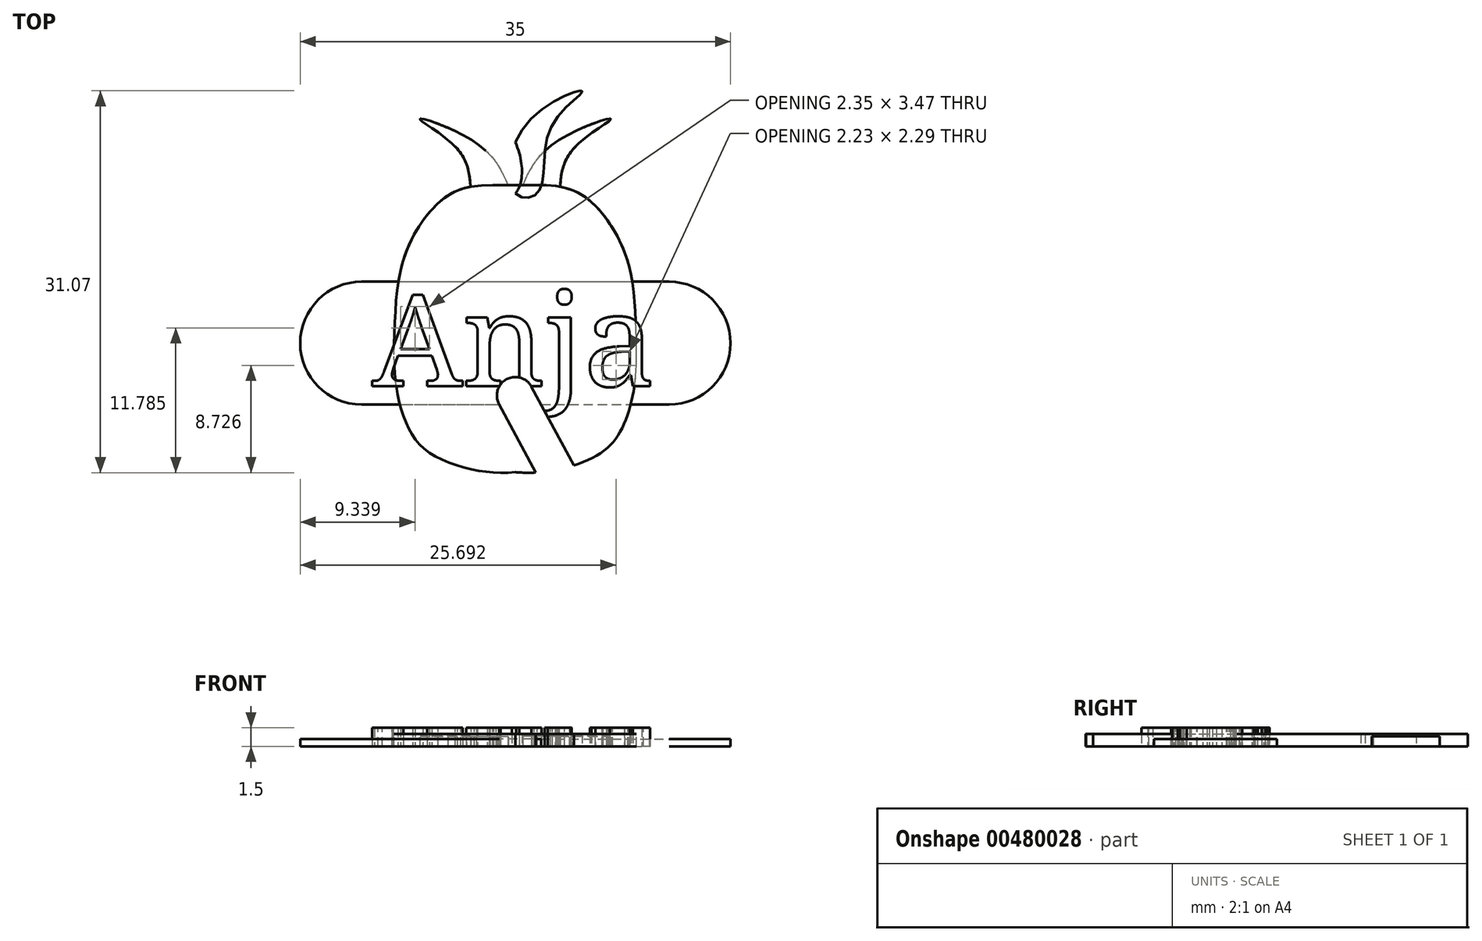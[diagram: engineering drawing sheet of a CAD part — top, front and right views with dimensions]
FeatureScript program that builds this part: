
annotation { "Feature Type Name" : "Feature", "Feature Type Description" : "" }
export const myFeature = defineFeature(function(context is Context, id is Id, definition is map)
    precondition{}
    {
        {
            var Q0;
            Q0=qCreatedBy(makeId("Top.planeOp"),FACE);
            var sketch = newSketch(context, id + "F0", { "sketchPlane" : qUnion([Q0])});
            skText(sketch, "E0", { "text": "Anja", "fontName": "NotoSerif-Regular.ttf"});
            const initialGuessF0  = {"E0": [-0.01164, -0.0075, 1, 0, 0.0075]};
            skSetInitialGuess(sketch, initialGuessF0);
            skSolve(sketch);
        }
        {
            var Q0;
            Q0 = qSketchRegion(id + "F0", true);
            extrude(context, id + "F1", {"entities" : qUnion([Q0]), "depth" : 1.5 * mm, "offsetDistance" : 25 * mm});
        }
        {
            var Q0;
            Q0=qCreatedBy(makeId("Top.planeOp"),FACE);
            var sketch = newSketch(context, id + "F2", { "sketchPlane" : qUnion([Q0])});
            skFitSpline(sketch, "E1", {"points": [v(0, -14.5) * mm, v(-3.65, -14.24) * mm, v(-7.11, -12.83) * mm, v(-8.78, -10.71) * mm, v(-9.74, -7.05) * mm, v(-9.8, -2.69) * mm, v(-9.49, 1.16) * mm, v(-8.52, 4.24) * mm, v(-6.73, 6.94) * mm, v(-4.16, 8.6) * mm, v(0, 8.86) * mm], "startDerivative": vector(-36.01, -3.1) * mm, "endDerivative": vector(39.07, 0.66) * mm});
            skFitSpline(sketch, "E2.MirrorCS", {"points": [v(0, -14.5) * mm, v(3.65, -14.24) * mm, v(7.11, -12.83) * mm, v(8.78, -10.71) * mm, v(9.74, -7.05) * mm, v(9.8, -2.69) * mm, v(9.49, 1.16) * mm, v(8.52, 4.24) * mm, v(6.73, 6.94) * mm, v(4.16, 8.6) * mm, v(0, 8.86) * mm], "startDerivative": vector(36.01, -3.1) * mm, "endDerivative": vector(-39.07, 0.66) * mm});
            skSolve(sketch);
        }
        {
            var Q0;
            Q0=makeQuery(id+"F2.imprint","IMPRINT",FACE,{"disambiguationData":[TD([[makeQuery(id+"F2.imprint","IMPRINT",EDGE,{"derivedFrom":sQuery(id+"F2.wireOp",EDGE,"E1")}),-1.0]])]});
            extrude(context, id + "F3", {"entities" : qUnion([Q0]), "depth" : 1 * mm, "offsetDistance" : 25 * mm});
        }
        {
            var Q0;
            Q0=qCreatedBy(makeId("Top.planeOp"),FACE);
            var sketch = newSketch(context, id + "F4", { "sketchPlane" : qUnion([Q0])});
            skFitSpline(sketch, "E3", {"points": [v(-3.62, 8.13) * mm, v(-4.76, 11.85) * mm, v(-7.76, 14.23) * mm, v(-3.16, 12.26) * mm, v(-0.47, 8.54) * mm], "startDerivative": vector(-0.55, 16.12) * mm, "endDerivative": vector(6.29, -15.12) * mm});
            skLineSegment(sketch, "E4", {"start": v(-3.62, 8.13) * mm, "end": v(-0.47, 8.54) * mm});
            skFitSpline(sketch, "E5.MirrorCS", {"points": [v(3.62, 8.13) * mm, v(4.76, 11.85) * mm, v(7.76, 14.23) * mm, v(3.16, 12.26) * mm, v(0.47, 8.54) * mm], "startDerivative": vector(0.55, 16.12) * mm, "endDerivative": vector(-6.29, -15.12) * mm});
            skLineSegment(sketch, "E6", {"start": v(0.47, 8.54) * mm, "end": v(3.62, 8.13) * mm});
            skSolve(sketch);
        }
        {
            var Q0;
            Q0=makeQuery(id+"F4.imprint","IMPRINT",FACE,{"disambiguationData":[TD([[makeQuery(id+"F4.imprint","IMPRINT",EDGE,{"derivedFrom":sQuery(id+"F4.wireOp",EDGE,"E3")}),-1.0]])]});
            var Q1;
            Q1=makeQuery(id+"F4.imprint","IMPRINT",FACE,{"disambiguationData":[TD([[makeQuery(id+"F4.imprint","IMPRINT",EDGE,{"derivedFrom":sQuery(id+"F4.wireOp",EDGE,"E5.MirrorCS")}),1.0]])]});
            extrude(context, id + "F5", {"entities" : qUnion([Q0, Q1]), "operationType" : NewBodyOperationType.ADD, "depth" : 0.8 * mm, "offsetDistance" : 25 * mm});
        }
        {
            var Q0;
            Q0=qCreatedBy(makeId("Top.planeOp"),FACE);
            var sketch = newSketch(context, id + "F6", { "sketchPlane" : qUnion([Q0])});
            skFitSpline(sketch, "E7", {"points": [v(-1.9, 8.32) * mm, v(-2.9, 13.55) * mm, v(-5.45, 16.5) * mm, v(-0.96, 13.88) * mm, v(0, 8.18) * mm, v(-1.9, 8.32) * mm]});
            skFitSpline(sketch, "E8.MirrorC", {"points": [v(1.9, 8.32) * mm, v(2.9, 13.55) * mm, v(5.45, 16.5) * mm, v(0.96, 13.88) * mm, v(0, 8.18) * mm, v(1.9, 8.32) * mm]});
            skSolve(sketch);
        }
        {
            var Q0;
            {var subQ0=sQuery(id+"F6.wireOp",EDGE,"E8.MirrorC");var subQ1=sQuery(id+"F6.wireOp",EDGE,"E7");var subQ2=makeQuery(id+"F6.imprint","INTERSECT",VERTEX,{"disambiguationData":[OD(0.0)],"derivedFrom":[subQ1,subQ0]});Q0=makeQuery(id+"F6.imprint","IMPRINT",FACE,{"disambiguationData":[TD([[makeQuery(id+"F6.imprint","IMPRINT",EDGE,{"disambiguationData":[TD([[subQ2,-1.0]])],"derivedFrom":subQ1}),-1.0]])]});}
            var Q1;
            {var subQ0=sQuery(id+"F6.wireOp",EDGE,"E8.MirrorC");var subQ1=sQuery(id+"F6.wireOp",EDGE,"E7");var subQ2=makeQuery(id+"F6.imprint","INTERSECT",VERTEX,{"disambiguationData":[OD(0.0)],"derivedFrom":[subQ1,subQ0]});Q1=makeQuery(id+"F6.imprint","IMPRINT",FACE,{"disambiguationData":[TD([[makeQuery(id+"F6.imprint","IMPRINT",EDGE,{"disambiguationData":[TD([[subQ2,1.0]])],"derivedFrom":subQ1}),1.0]])]});}
            extrude(context, id + "F7", {"entities" : qUnion([Q0, Q1]), "depth" : 1 * mm, "offsetDistance" : 25 * mm});
        }
        {
            var Q0;
            Q0=qCreatedBy(makeId("Top.planeOp"),FACE);
            var sketch = newSketch(context, id + "F8", { "sketchPlane" : qUnion([Q0])});
            skLineSegment(sketch, "E9.bottom", {"start": v(-12.5, 1) * mm, "end": v(12.5, 1) * mm});
            skLineSegment(sketch, "E9.top", {"start": v(-12.5, -9) * mm, "end": v(12.5, -9) * mm});
            skArc(sketch, "E10", {"start": v(-12.5, -9) * mm, "mid": v(-17.5, -4) * mm, "end": v(-12.5, 1) * mm});
            skArc(sketch, "E11", {"start": v(12.5, -9) * mm, "mid": v(17.5, -4) * mm, "end": v(12.5, 1) * mm});
            skSolve(sketch);
        }
        {
            var Q0;
            Q0=makeQuery(id+"F8.imprint","IMPRINT",FACE,{"disambiguationData":[TD([[makeQuery(id+"F8.imprint","IMPRINT",EDGE,{"derivedFrom":sQuery(id+"F8.wireOp",EDGE,"E9.bottom")}),-1.0]])]});
            extrude(context, id + "F9", {"entities" : qUnion([Q0]), "depth" : 0.6 * mm, "offsetDistance" : 25 * mm});
        }
        {
            var Q0;
            Q0=qCreatedBy(makeId("Top.planeOp"),FACE);
            var sketch = newSketch(context, id + "F10", { "sketchPlane" : qUnion([Q0])});
            skLineSegment(sketch, "E12", {"start": v(3.92, -18.7) * mm, "end": v(-1.32, -8.97) * mm});
            skLineSegment(sketch, "E13", {"start": v(-1.32, -8.97) * mm, "end": v(1.32, -7.55) * mm, "construction": true});
            skLineSegment(sketch, "E14", {"start": v(1.32, -7.55) * mm, "end": v(6.54, -17.23) * mm});
            skLineSegment(sketch, "E15", {"start": v(6.54, -17.23) * mm, "end": v(3.92, -18.7) * mm});
            skArc(sketch, "E16", {"start": v(-1.32, -8.97) * mm, "mid": v(-0.71, -6.94) * mm, "end": v(1.32, -7.55) * mm});
            skSolve(sketch);
        }
        {
            var Q0;
            Q0=makeQuery(id+"F10.imprint","IMPRINT",FACE,{"disambiguationData":[TD([[makeQuery(id+"F10.imprint","IMPRINT",EDGE,{"derivedFrom":sQuery(id+"F10.wireOp",EDGE,"E12")}),-1.0]])]});
            extrude(context, id + "F11", {"entities" : qUnion([Q0]), "operationType" : NewBodyOperationType.REMOVE, "depth" : 25 * mm, "offsetDistance" : 25 * mm});
        }
    });
